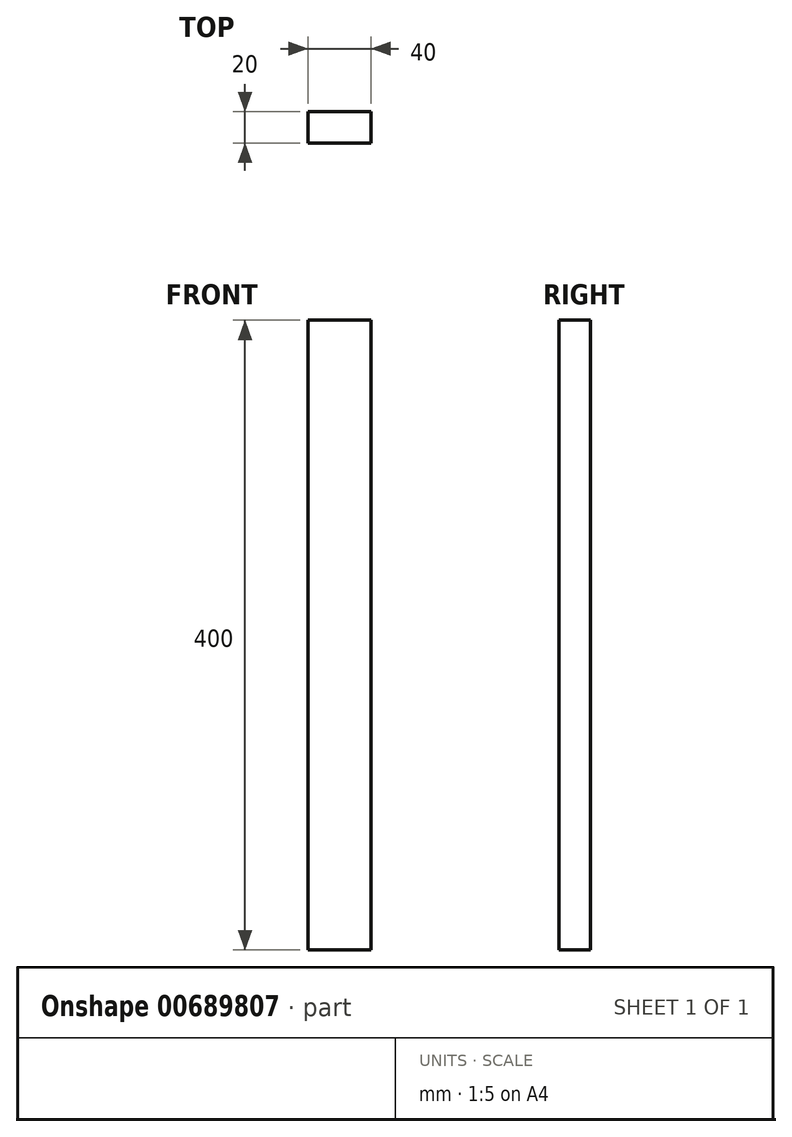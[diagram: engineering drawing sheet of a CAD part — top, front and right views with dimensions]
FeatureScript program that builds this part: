
annotation { "Feature Type Name" : "Feature", "Feature Type Description" : "" }
export const myFeature = defineFeature(function(context is Context, id is Id, definition is map)
    precondition{}
    {
        {
            var Q0;
            Q0=qCreatedBy(makeId("Top.planeOp"),FACE);
            var sketch = newSketch(context, id + "F0", { "sketchPlane" : qUnion([Q0])});
            skLineSegment(sketch, "E0.bottom", {"start": v(0, 0) * mm, "end": v(40, 0) * mm});
            skLineSegment(sketch, "E0.top", {"start": v(0, 20) * mm, "end": v(40, 20) * mm});
            skLineSegment(sketch, "E0.left", {"start": v(0, 0) * mm, "end": v(0, 20) * mm});
            skLineSegment(sketch, "E0.right", {"start": v(40, 0) * mm, "end": v(40, 20) * mm});
            skSolve(sketch);
        }
        {
            var Q0;
            Q0=makeQuery(id+"F0.imprint","IMPRINT",FACE,{"disambiguationData":[TD([[makeQuery(id+"F0.imprint","IMPRINT",EDGE,{"derivedFrom":sQuery(id+"F0.wireOp",EDGE,"E0.bottom")}),1.0]])]});
            extrude(context, id + "F1", {"entities" : qUnion([Q0]), "depth" : 400 * mm, "offsetDistance" : 25 * mm});
        }
    });
